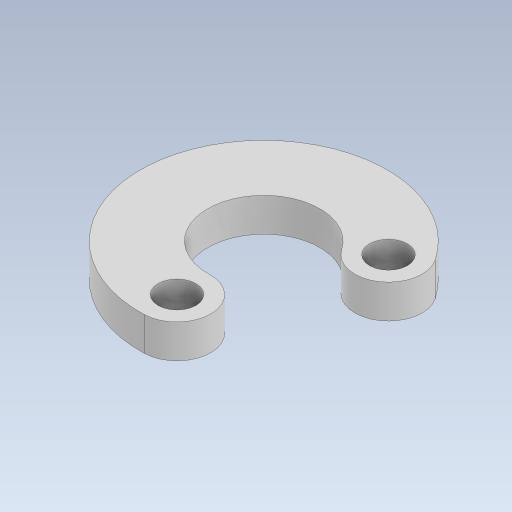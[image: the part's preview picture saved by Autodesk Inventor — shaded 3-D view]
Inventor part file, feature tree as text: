
AUTODESK INVENTOR PART (.ipt)
format: ipt  version: 2023 (Build 270158000, 158)  size: 120,832 bytes
history: native  units: in
note: dims shown in document units (in); Inventor stores cm internally (conversion verified against a paired STEP export)
features: sketch x2, extrude x1, hole x1
ambient origin geometry x8: Origin, YZ Plane, XZ Plane, XY Plane, X Axis, Y Axis, Z Axis, Center Point
bodies: Solid1 (feature_tree)
feature tree (4):
  extrude  "Extrusion1"  Depth=0.5in
  hole  "Hole1"  [1 undecoded]
  sketch  "Sketch1"  dims[d0=0.4724in d1=0.5in]
  sketch  "Sketch2"  dims[d2=0.9843in d3=135.0deg d4=0.2362in d5=0.0in d6=0.2362in d7=0.266in d8=0.2362in d9=0.507in d10=0.0787in d11=0.5635in d12=0.5in d13=0.8108in d14=0.3937in]
note: 1 required parameter value undecoded (feature->parameter linkage not recoverable at this tier; creation-order binding heuristic only, values carry confidence <= 0.55)
